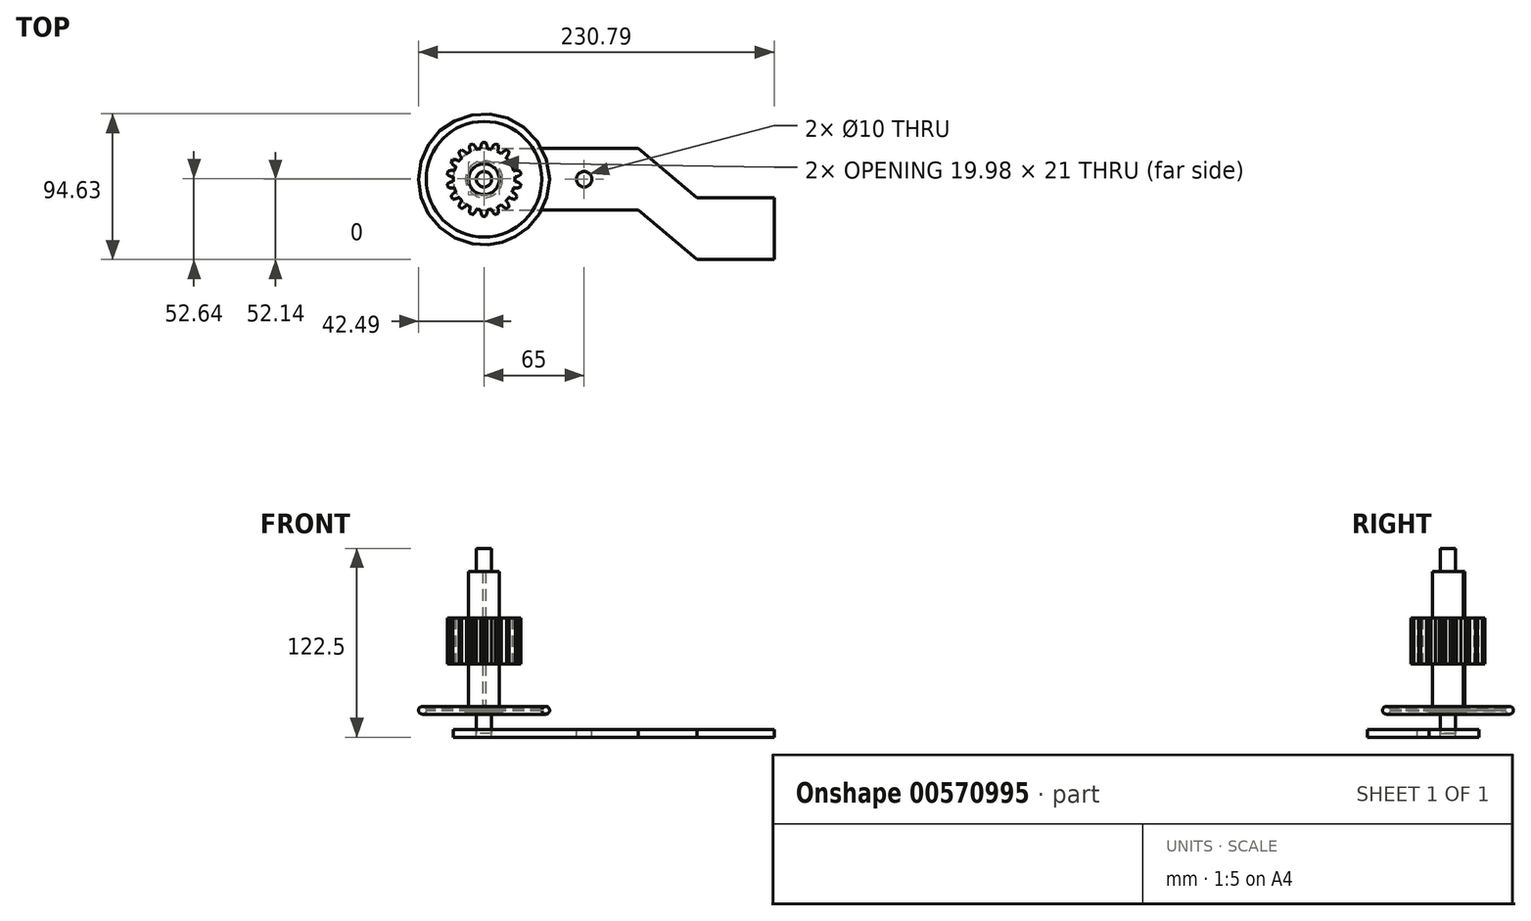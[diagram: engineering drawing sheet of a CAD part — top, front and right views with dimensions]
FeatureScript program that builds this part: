
annotation { "Feature Type Name" : "Feature", "Feature Type Description" : "" }
export const myFeature = defineFeature(function(context is Context, id is Id, definition is map)
    precondition{}
    {
        {
            var Q0;
            Q0=qCreatedBy(makeId("Top.planeOp"),FACE);
            var sketch = newSketch(context, id + "F0", { "sketchPlane" : qUnion([Q0])});
            skArc(sketch, "E0", {"start": v(-2, 19.9) * mm, "mid": v(0, -20) * mm, "end": v(2, 19.9) * mm});
            skLineSegment(sketch, "E1", {"start": v(-1, 24) * mm, "end": v(1, 24) * mm});
            skArc(sketch, "E2", {"start": v(2, 19.9) * mm, "mid": v(1.87, 22.04) * mm, "end": v(1, 24) * mm});
            skArc(sketch, "E3", {"start": v(-1, 24) * mm, "mid": v(-1.87, 22.04) * mm, "end": v(-2, 19.9) * mm});
            skCircle(sketch, "E4", {"center": v(0, 0) * mm, "radius": 10 * mm});
            skLineSegment(sketch, "E5.bottom", {"start": v(1, 9) * mm, "end": v(-1, 9) * mm});
            skLineSegment(sketch, "E5.top", {"start": v(1, 11) * mm, "end": v(-1, 11) * mm});
            skLineSegment(sketch, "E5.left", {"start": v(1, 9) * mm, "end": v(1, 11) * mm});
            skLineSegment(sketch, "E5.right", {"start": v(-1, 9) * mm, "end": v(-1, 11) * mm});
            skPoint(sketch, "E5.middle", {"position": v(0, 10) * mm});
            skCircle(sketch, "E6", {"center": v(0, 0) * mm, "radius": 5 * mm});
            skSolve(sketch);
        }
        {
            var Q0;
            Q0=makeQuery(id+"F0.imprint","IMPRINT",FACE,{"disambiguationData":[TD([[makeQuery(id+"F0.imprint","IMPRINT",EDGE,{"derivedFrom":sQuery(id+"F0.wireOp",EDGE,"E0")}),1.0]])]});
            extrude(context, id + "F1", {"entities" : qUnion([Q0]), "depth" : 30 * mm, "offsetDistance" : 25 * mm, "symmetric" : true});
        }
        {
            var Q0;
            Q0=makeQuery(id+"F0.imprint","IMPRINT",FACE,{"disambiguationData":[TD([[makeQuery(id+"F0.imprint","IMPRINT",EDGE,{"derivedFrom":sQuery(id+"F0.wireOp",EDGE,"E6")}),1.0]])]});
            extrude(context, id + "F2", {"entities" : qUnion([Q0]), "depth" : 120 * mm, "offsetDistance" : 25 * mm, "symmetric" : true});
        }
        {
            var Q0;
            Q0=makeQuery(id+"F1.opExtrude","SWEPT_BODY",BODY,{"disambiguationData":[OSD([sQuery(id+"F0.wireOp",EDGE,"E0"),sQuery(id+"F0.wireOp",EDGE,"E1"),sQuery(id+"F0.wireOp",EDGE,"E2"),sQuery(id+"F0.wireOp",EDGE,"E3")])]});
            var Q1;
            Q1=makeQuery(id+"F1.opExtrude","SWEPT_FACE",FACE,{"disambiguationData":[OSD([sQuery(id+"F0.wireOp",EDGE,"E0")])]});
            circularPattern(context, id + "F3", {"operationType" : NewBodyOperationType.ADD, "entities" : qUnion([Q0]), "axis" : qUnion([Q1]), "angle" : 360 * degree, "instanceCount" : 18, "equalSpace" : true});
        }
        {
            var Q0;
            Q0=makeQuery(id+"F0.imprint","IMPRINT",FACE,{"disambiguationData":[TD([[makeQuery(id+"F0.imprint","IMPRINT",EDGE,{"derivedFrom":sQuery(id+"F0.wireOp",EDGE,"E4")}),1.0]])]});
            var Q1;
            {var subQ5=sQuery(id+"F0.wireOp",EDGE,"E5.top");Q1=makeQuery(id+"F0.imprint","IMPRINT",FACE,{"disambiguationData":[TD([[makeQuery(id+"F0.imprint","IMPRINT",EDGE,{"derivedFrom":subQ5}),1.0]])]});}
            var Q2;
            {var subQ1=sQuery(id+"F0.wireOp",EDGE,"E5.bottom");Q2=makeQuery(id+"F0.imprint","IMPRINT",FACE,{"disambiguationData":[TD([[makeQuery(id+"F0.imprint","IMPRINT",EDGE,{"derivedFrom":subQ1}),1.0]])]});}
            extrude(context, id + "F4", {"entities" : qUnion([Q0, Q1, Q2]), "operationType" : NewBodyOperationType.ADD, "depth" : 90 * mm, "offsetDistance" : 25 * mm, "symmetric" : true});
        }
        {
            var Q0;
            Q0=makeQuery(id+"F4.opExtrude","CAP_FACE",FACE,{"disambiguationData":[OSD([sQuery(id+"F0.wireOp",EDGE,"E4"),sQuery(id+"F0.wireOp",EDGE,"E5.top"),sQuery(id+"F0.wireOp",EDGE,"E5.left"),sQuery(id+"F0.wireOp",EDGE,"E5.right")])],"isStart":true});
            var sketch = newSketch(context, id + "F5", { "sketchPlane" : qUnion([Q0])});
            skCircle(sketch, "E7", {"center": v(0, 0) * mm, "radius": 40 * mm});
            skSolve(sketch);
        }
        {
            var Q0;
            Q0=qCreatedBy(makeId("Front.planeOp"),FACE);
            var sketch = newSketch(context, id + "F6", { "sketchPlane" : qUnion([Q0])});
            skCircle(sketch, "E8", {"center": v(-39.99, -45) * mm, "radius": 2.5 * mm});
            skLineSegment(sketch, "E9", {"start": v(-10, -45) * mm, "end": v(-10, -15) * mm});
            skLineSegment(sketch, "E10", {"start": v(10, -15) * mm, "end": v(10, -45) * mm});
            skLineSegment(sketch, "E11", {"start": v(-10, -43.59) * mm, "end": v(-12, -43.59) * mm});
            skLineSegment(sketch, "E12", {"start": v(-12, -43.59) * mm, "end": v(-12, -44.59) * mm});
            skLineSegment(sketch, "E13", {"start": v(-12, -44.59) * mm, "end": v(-37.52, -44.59) * mm});
            skLineSegment(sketch, "E14", {"start": v(-45.29, -45) * mm, "end": v(23.03, -45) * mm, "construction": true});
            skLineSegment(sketch, "E15.MirrorCS", {"start": v(-12, -45.41) * mm, "end": v(-37.52, -45.41) * mm});
            skLineSegment(sketch, "E16.MirrorCS", {"start": v(-12, -46.41) * mm, "end": v(-12, -45.41) * mm});
            skLineSegment(sketch, "E17.MirrorCS", {"start": v(-10, -46.41) * mm, "end": v(-12, -46.41) * mm});
            skLineSegment(sketch, "E18", {"start": v(-10, -43.59) * mm, "end": v(-10, -46.41) * mm});
            skSolve(sketch);
        }
        {
            var Q0;
            {var subQ0=sQuery(id+"F6.wireOp",EDGE,"E8");var subQ1=makeQuery(id+"F6.imprint","INTERSECT",VERTEX,{"derivedFrom":[subQ0,sQuery(id+"F6.wireOp",EDGE,"E13")]});Q0=makeQuery(id+"F6.imprint","IMPRINT",FACE,{"disambiguationData":[TD([[makeQuery(id+"F6.imprint","IMPRINT",EDGE,{"disambiguationData":[TD([[subQ1,-1.0]])],"derivedFrom":subQ0}),1.0]])]});}
            var Q1;
            {var subQ1=sQuery(id+"F6.wireOp",EDGE,"E11");Q1=makeQuery(id+"F6.imprint","IMPRINT",FACE,{"disambiguationData":[TD([[makeQuery(id+"F6.imprint","IMPRINT",EDGE,{"derivedFrom":subQ1}),1.0]])]});}
            var Q2;
            Q2=sQuery(id+"F5.wireOp",EDGE,"E7");
            revolve(context, id + "F7", {"entities" : qUnion([Q0, Q1]), "axis" : qUnion([Q2]), "revolveType" : RevolveType.FULL});
        }
        {
            var Q0;
            Q0=makeQuery(id+"F7.opRevolve","SWEPT_FACE",FACE,{"disambiguationData":[OSD([sQuery(id+"F6.wireOp",EDGE,"E15.MirrorCS")])]});
            var sketch = newSketch(context, id + "F8", { "sketchPlane" : qUnion([Q0])});
            skArc(sketch, "E19.0.0", {"start": v(1, -9.95) * mm, "mid": v(0, 10) * mm, "end": v(-1, -9.95) * mm});
            skLineSegment(sketch, "E19.0.1", {"start": v(-1, -9.95) * mm, "end": v(-1, -11) * mm});
            skLineSegment(sketch, "E19.0.2", {"start": v(-1, -11) * mm, "end": v(1, -11) * mm});
            skLineSegment(sketch, "E19.0.3", {"start": v(1, -11) * mm, "end": v(1, -9.95) * mm});
            skLineSegment(sketch, "E20.bottom", {"start": v(-1, -9) * mm, "end": v(1, -9) * mm});
            skLineSegment(sketch, "E20.left", {"start": v(-1, -9) * mm, "end": v(-1, -11) * mm});
            skLineSegment(sketch, "E20.right", {"start": v(1, -9) * mm, "end": v(1, -11) * mm});
            skPoint(sketch, "E20.middle", {"position": v(0, -10) * mm});
            skPoint(sketch, "E20.middle.positionSnap0", {"position": v(0, -11) * mm});
            skPoint(sketch, "E20.centerSnap0", {"position": v(0, -11) * mm});
            skSolve(sketch);
        }
        {
            var Q0;
            {var subQ4=sQuery(id+"F8.wireOp",EDGE,"E20.bottom");Q0=makeQuery(id+"F8.imprint","IMPRINT",FACE,{"disambiguationData":[TD([[makeQuery(id+"F8.imprint","IMPRINT",EDGE,{"derivedFrom":subQ4}),-1.0]])]});}
            extrude(context, id + "F9", {"entities" : qUnion([Q0]), "operationType" : NewBodyOperationType.REMOVE, "oppositeDirection" : true, "depth" : 7.8 * mm, "offsetDistance" : 25 * mm, "symmetric" : true});
        }
        {
            var Q0;
            Q0=makeQuery(id+"F2.opExtrude","CAP_FACE",FACE,{"disambiguationData":[OSD([sQuery(id+"F0.wireOp",EDGE,"E6")])],"isStart":true});
            var sketch = newSketch(context, id + "F10", { "sketchPlane" : qUnion([Q0])});
            skCircle(sketch, "E21", {"center": v(0, 0) * mm, "radius": 20 * mm});
            skCircle(sketch, "E22", {"center": v(0, 0) * mm, "radius": 5 * mm});
            skLineSegment(sketch, "E23", {"start": v(0, 20) * mm, "end": v(100, 20) * mm});
            skLineSegment(sketch, "E24", {"start": v(0, -20) * mm, "end": v(100, -20) * mm});
            skLineSegment(sketch, "E25", {"start": v(100, -20) * mm, "end": v(138.3, 12.14) * mm});
            skLineSegment(sketch, "E26", {"start": v(100, 20) * mm, "end": v(138.3, 52.14) * mm});
            skLineSegment(sketch, "E27", {"start": v(138.3, 12.14) * mm, "end": v(188.3, 12.14) * mm});
            skLineSegment(sketch, "E28", {"start": v(188.3, 12.14) * mm, "end": v(188.3, 52.14) * mm});
            skLineSegment(sketch, "E29", {"start": v(188.3, 52.14) * mm, "end": v(138.3, 52.14) * mm});
            skCircle(sketch, "E30", {"center": v(65, 0) * mm, "radius": 5 * mm});
            skSolve(sketch);
        }
        {
            var Q0;
            Q0 = qSketchRegion(id + "F10", true);
            extrude(context, id + "F11", {"entities" : qUnion([Q0]), "depth" : 5 * mm, "offsetDistance" : 25 * mm, "symmetric" : true});
        }
    });
